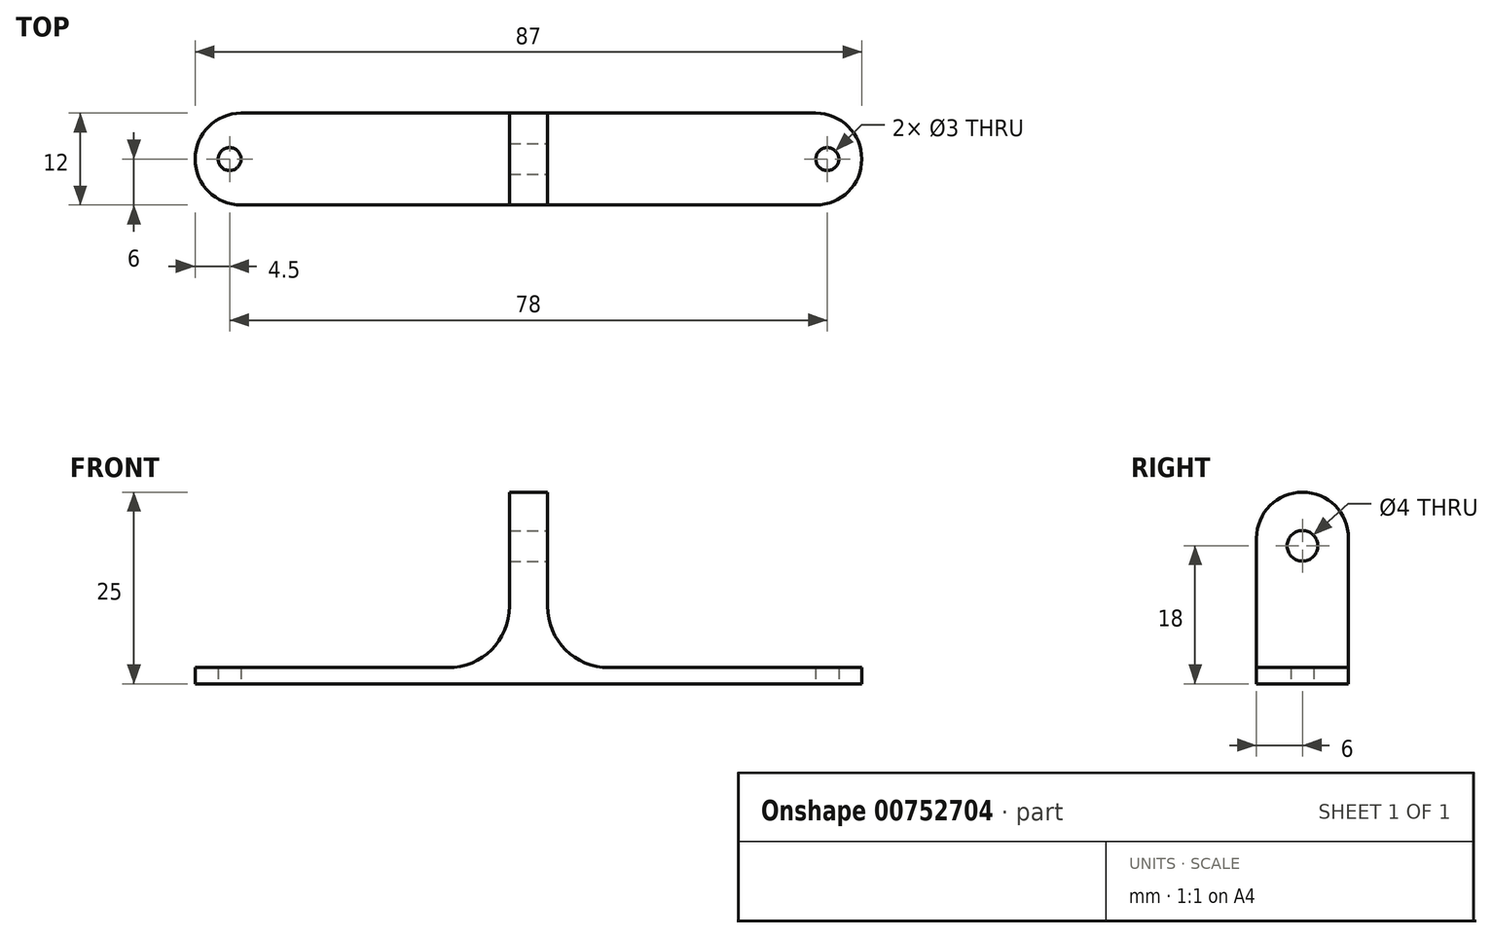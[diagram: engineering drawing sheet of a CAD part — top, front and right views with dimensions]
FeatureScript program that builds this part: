
annotation { "Feature Type Name" : "Feature", "Feature Type Description" : "" }
export const myFeature = defineFeature(function(context is Context, id is Id, definition is map)
    precondition{}
    {
        {
            var Q0;
            Q0=qCreatedBy(makeId("Top.planeOp"),FACE);
            var sketch = newSketch(context, id + "F0", { "sketchPlane" : qUnion([Q0])});
            skLineSegment(sketch, "E0.bottom", {"start": v(-43.5, -6) * mm, "end": v(43.5, -6) * mm});
            skLineSegment(sketch, "E0.top", {"start": v(-43.5, 6) * mm, "end": v(43.5, 6) * mm});
            skLineSegment(sketch, "E0.left", {"start": v(-43.5, -6) * mm, "end": v(-43.5, 6) * mm});
            skLineSegment(sketch, "E0.right", {"start": v(43.5, -6) * mm, "end": v(43.5, 6) * mm});
            skPoint(sketch, "E0.middle", {"position": v(0, 0) * mm});
            skLineSegment(sketch, "E1", {"start": v(0, 0) * mm, "end": v(-39, 0) * mm, "construction": true});
            skCircle(sketch, "E2", {"center": v(-39, 0) * mm, "radius": 1.5 * mm});
            skLineSegment(sketch, "E3", {"start": v(0, 0) * mm, "end": v(0, -2.7) * mm, "construction": true});
            skCircle(sketch, "E4.MirrorC", {"center": v(39, 0) * mm, "radius": 1.5 * mm});
            skLineSegment(sketch, "E5.bottom", {"start": v(-2.5, -6) * mm, "end": v(2.5, -6) * mm});
            skLineSegment(sketch, "E5.top", {"start": v(-2.5, 6) * mm, "end": v(2.5, 6) * mm});
            skLineSegment(sketch, "E5.left", {"start": v(-2.5, -6) * mm, "end": v(-2.5, 6) * mm});
            skLineSegment(sketch, "E5.right", {"start": v(2.5, -6) * mm, "end": v(2.5, 6) * mm});
            skSolve(sketch);
        }
        {
            var Q0;
            {var subQ0=sQuery(id+"F0.wireOp",EDGE,"E0.right");var subQ7=sQuery(id+"F0.wireOp",EDGE,"E5.left");var subQ10=makeQuery(id+"F0.imprint","IMPRINT",EDGE,{"derivedFrom":subQ7});var subQ11=sQuery(id+"F0.wireOp",EDGE,"E0.left");Q0=qUnion([makeQuery(id+"F0.imprint","IMPRINT",FACE,{"disambiguationData":[TD([[makeQuery(id+"F0.imprint","IMPRINT",EDGE,{"derivedFrom":subQ11}),-1.0]])]}),makeQuery(id+"F0.imprint","IMPRINT",FACE,{"disambiguationData":[TD([[subQ10,-1.0]])]}),makeQuery(id+"F0.imprint","IMPRINT",FACE,{"disambiguationData":[TD([[makeQuery(id+"F0.imprint","IMPRINT",EDGE,{"derivedFrom":subQ0}),1.0]])]})]);}
            extrude(context, id + "F1", {"entities" : qUnion([Q0]), "depth" : 2.1 * mm, "offsetDistance" : 25 * mm});
        }
        {
            var Q0;
            {var subQ2=sQuery(id+"F0.wireOp",EDGE,"E5.left");Q0=makeQuery(id+"F0.imprint","IMPRINT",FACE,{"disambiguationData":[TD([[makeQuery(id+"F0.imprint","IMPRINT",EDGE,{"derivedFrom":subQ2}),-1.0]])]});}
            extrude(context, id + "F2", {"entities" : qUnion([Q0]), "operationType" : NewBodyOperationType.ADD, "depth" : 25 * mm, "offsetDistance" : 25 * mm});
        }
        {
            var Q0;
            Q0=qCreatedBy(makeId("Right.planeOp"),FACE);
            var sketch = newSketch(context, id + "F3", { "sketchPlane" : qUnion([Q0])});
            skLineSegment(sketch, "E6", {"start": v(0, 0) * mm, "end": v(0, 18) * mm, "construction": true});
            skCircle(sketch, "E7", {"center": v(0, 18) * mm, "radius": 2 * mm});
            skSolve(sketch);
        }
        {
            var Q0;
            Q0 = qSketchRegion(id + "F3", true);
            extrude(context, id + "F4", {"entities" : qUnion([Q0]), "operationType" : NewBodyOperationType.REMOVE, "endBound" : BoundingType.SYMMETRIC, "oppositeDirection" : true, "depth" : 25 * mm, "offsetDistance" : 25 * mm});
        }
        {
            var Q0;
            Q0=makeQuery(id+"F2.opExtrude","CAP_EDGE",EDGE,{"disambiguationData":[OSD([sQuery(id+"F0.wireOp",EDGE,"E0.bottom")])],"isStart":false});
            var Q1;
            Q1=makeQuery(id+"F2.opExtrude","CAP_EDGE",EDGE,{"disambiguationData":[OSD([sQuery(id+"F0.wireOp",EDGE,"E0.top")])],"isStart":false});
            var Q2;
            Q2=makeQuery(id+"F1.opExtrude","SWEPT_EDGE",EDGE,{"disambiguationData":[OSD([sQuery(id+"F0.wireOp",EDGE,"E0.bottom"),sQuery(id+"F0.wireOp",EDGE,"E0.left")])]});
            var Q3;
            Q3=makeQuery(id+"F1.opExtrude","SWEPT_EDGE",EDGE,{"disambiguationData":[OSD([sQuery(id+"F0.wireOp",EDGE,"E0.top"),sQuery(id+"F0.wireOp",EDGE,"E0.left")])]});
            var Q4;
            Q4=makeQuery(id+"F1.opExtrude","SWEPT_EDGE",EDGE,{"disambiguationData":[OSD([sQuery(id+"F0.wireOp",EDGE,"E0.bottom"),sQuery(id+"F0.wireOp",EDGE,"E0.right")])]});
            var Q5;
            Q5=makeQuery(id+"F1.opExtrude","SWEPT_EDGE",EDGE,{"disambiguationData":[OSD([sQuery(id+"F0.wireOp",EDGE,"E0.top"),sQuery(id+"F0.wireOp",EDGE,"E0.right")])]});
            fillet(context, id + "F5", {"entities" : qUnion([Q0, Q1, Q2, Q3, Q4, Q5]), "radius" : 6 * mm, "tangentPropagation" : true, "allowEdgeOverflow" : false});
        }
        {
            var Q0;
            Q0=makeQuery(id+"F2.boolean.opBoolean","INTERSECT",EDGE,{"derivedFrom":[makeQuery(id+"F1.opExtrude","CAP_FACE",FACE,{"disambiguationData":[OSD([sQuery(id+"F0.wireOp",EDGE,"E0.bottom"),sQuery(id+"F0.wireOp",EDGE,"E0.top"),sQuery(id+"F0.wireOp",EDGE,"E0.left"),sQuery(id+"F0.wireOp",EDGE,"E0.right"),sQuery(id+"F0.wireOp",EDGE,"E2"),sQuery(id+"F0.wireOp",EDGE,"E4.MirrorC")])],"isStart":false}),makeQuery(id+"F2.opExtrude","SWEPT_FACE",FACE,{"disambiguationData":[OSD([sQuery(id+"F0.wireOp",EDGE,"E5.right")])]})]});
            var Q1;
            Q1=makeQuery(id+"F2.boolean.opBoolean","INTERSECT",EDGE,{"derivedFrom":[makeQuery(id+"F1.opExtrude","CAP_FACE",FACE,{"disambiguationData":[OSD([sQuery(id+"F0.wireOp",EDGE,"E0.bottom"),sQuery(id+"F0.wireOp",EDGE,"E0.top"),sQuery(id+"F0.wireOp",EDGE,"E0.left"),sQuery(id+"F0.wireOp",EDGE,"E0.right"),sQuery(id+"F0.wireOp",EDGE,"E2"),sQuery(id+"F0.wireOp",EDGE,"E4.MirrorC")])],"isStart":false}),makeQuery(id+"F2.opExtrude","SWEPT_FACE",FACE,{"disambiguationData":[OSD([sQuery(id+"F0.wireOp",EDGE,"E5.left")])]})]});
            fillet(context, id + "F6", {"entities" : qUnion([Q0, Q1]), "radius" : 8 * mm, "tangentPropagation" : true, "allowEdgeOverflow" : false});
        }
    });
